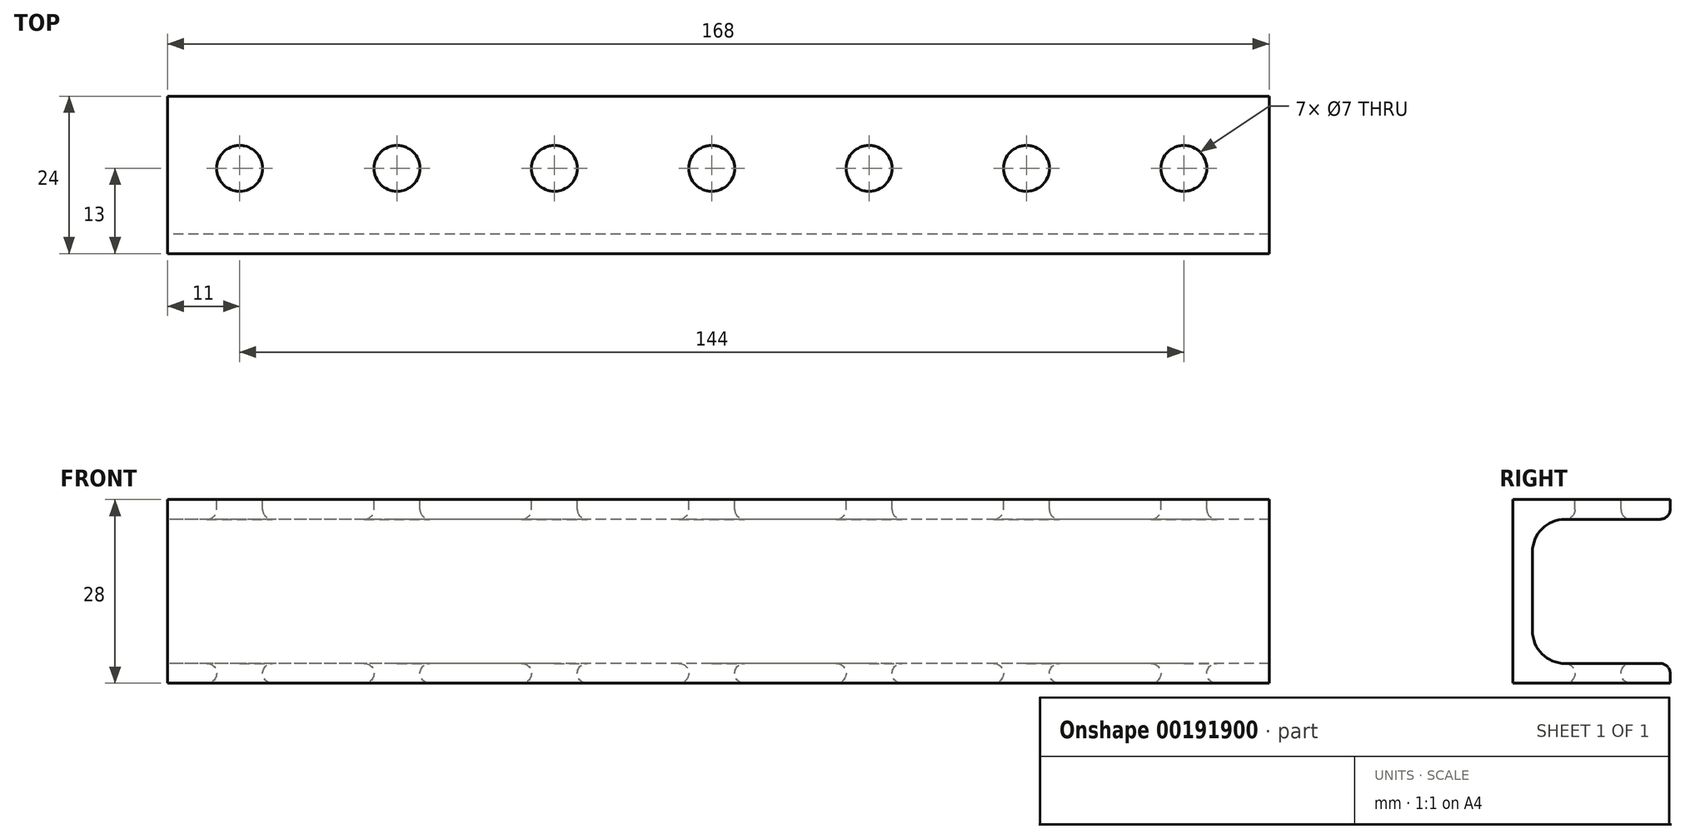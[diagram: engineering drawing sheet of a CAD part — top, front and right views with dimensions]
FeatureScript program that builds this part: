
annotation { "Feature Type Name" : "Feature", "Feature Type Description" : "" }
export const myFeature = defineFeature(function(context is Context, id is Id, definition is map)
    precondition{}
    {
        {
            var Q0;
            Q0=qCreatedBy(makeId("Right.planeOp"),FACE);
            var sketch = newSketch(context, id + "F0", { "sketchPlane" : qUnion([Q0])});
            skLineSegment(sketch, "E0", {"start": v(0, 27.91) * mm, "end": v(24, 27.91) * mm});
            skLineSegment(sketch, "E1", {"start": v(24, 27.91) * mm, "end": v(24, 24.91) * mm});
            skLineSegment(sketch, "E2", {"start": v(24, 24.91) * mm, "end": v(3, 24.91) * mm});
            skLineSegment(sketch, "E3", {"start": v(3, 24.91) * mm, "end": v(3, 2.91) * mm});
            skLineSegment(sketch, "E4", {"start": v(3, 2.91) * mm, "end": v(24, 2.91) * mm});
            skLineSegment(sketch, "E5", {"start": v(24, 2.91) * mm, "end": v(24, -0.09) * mm});
            skLineSegment(sketch, "E6", {"start": v(24, -0.09) * mm, "end": v(0, -0.09) * mm});
            skLineSegment(sketch, "E7", {"start": v(0, -0.09) * mm, "end": v(0, 0) * mm});
            skLineSegment(sketch, "E8", {"start": v(0, 27.91) * mm, "end": v(0, -0.09) * mm});
            skSolve(sketch);
        }
        {
            var Q0;
            {var subQ0=sQuery(id+"F0.wireOp",EDGE,"E0");Q0=makeQuery(id+"F0.imprint","IMPRINT",FACE,{"disambiguationData":[TD([[makeQuery(id+"F0.imprint","IMPRINT",EDGE,{"derivedFrom":subQ0}),-1.0]])]});}
            extrude(context, id + "F1", {"entities" : qUnion([Q0]), "depth" : 168 * mm});
        }
        {
            var Q0;
            Q0=makeQuery(id+"F1.opExtrude","SWEPT_FACE",FACE,{"disambiguationData":[OSD([sQuery(id+"F0.wireOp",EDGE,"E0")])]});
            var sketch = newSketch(context, id + "F2", { "sketchPlane" : qUnion([Q0])});
            skCircle(sketch, "E9", {"center": v(11, 13) * mm, "radius": 3.5 * mm});
            skCircle(sketch, "E10.1.0.0", {"center": v(35, 13) * mm, "radius": 3.5 * mm});
            skCircle(sketch, "E10.2.0.0", {"center": v(59, 13) * mm, "radius": 3.5 * mm});
            skCircle(sketch, "E10.3.0.0", {"center": v(83, 13) * mm, "radius": 3.5 * mm});
            skCircle(sketch, "E10.4.0.0", {"center": v(107, 13) * mm, "radius": 3.5 * mm});
            skCircle(sketch, "E10.5.0.0", {"center": v(131, 13) * mm, "radius": 3.5 * mm});
            skCircle(sketch, "E10.6.0.0", {"center": v(155, 13) * mm, "radius": 3.5 * mm});
            skLineSegment(sketch, "E10.direction1", {"start": v(11, 13) * mm, "end": v(35, 13) * mm, "construction": true});
            skSolve(sketch);
        }
        {
            var Q0;
            Q0=makeQuery(id+"F2.imprint","IMPRINT",FACE,{"disambiguationData":[TD([[makeQuery(id+"F2.imprint","IMPRINT",EDGE,{"derivedFrom":sQuery(id+"F2.wireOp",EDGE,"E9")}),1.0]])]});
            var Q1;
            Q1=makeQuery(id+"F2.imprint","IMPRINT",FACE,{"disambiguationData":[TD([[makeQuery(id+"F2.imprint","IMPRINT",EDGE,{"derivedFrom":sQuery(id+"F2.wireOp",EDGE,"E10.1.0.0")}),1.0]])]});
            var Q2;
            Q2=makeQuery(id+"F2.imprint","IMPRINT",FACE,{"disambiguationData":[TD([[makeQuery(id+"F2.imprint","IMPRINT",EDGE,{"derivedFrom":sQuery(id+"F2.wireOp",EDGE,"E10.2.0.0")}),1.0]])]});
            var Q3;
            Q3=makeQuery(id+"F2.imprint","IMPRINT",FACE,{"disambiguationData":[TD([[makeQuery(id+"F2.imprint","IMPRINT",EDGE,{"derivedFrom":sQuery(id+"F2.wireOp",EDGE,"E10.3.0.0")}),1.0]])]});
            var Q4;
            Q4=makeQuery(id+"F2.imprint","IMPRINT",FACE,{"disambiguationData":[TD([[makeQuery(id+"F2.imprint","IMPRINT",EDGE,{"derivedFrom":sQuery(id+"F2.wireOp",EDGE,"E10.4.0.0")}),1.0]])]});
            var Q5;
            Q5=makeQuery(id+"F2.imprint","IMPRINT",FACE,{"disambiguationData":[TD([[makeQuery(id+"F2.imprint","IMPRINT",EDGE,{"derivedFrom":sQuery(id+"F2.wireOp",EDGE,"E10.5.0.0")}),1.0]])]});
            var Q6;
            Q6=makeQuery(id+"F2.imprint","IMPRINT",FACE,{"disambiguationData":[TD([[makeQuery(id+"F2.imprint","IMPRINT",EDGE,{"derivedFrom":sQuery(id+"F2.wireOp",EDGE,"E10.6.0.0")}),1.0]])]});
            extrude(context, id + "F3", {"entities" : qUnion([Q0, Q1, Q2, Q3, Q4, Q5, Q6]), "operationType" : NewBodyOperationType.REMOVE, "oppositeDirection" : true, "depth" : 33 * mm});
        }
        {
            var Q0;
            Q0=makeQuery(id+"F1.opExtrude","SWEPT_EDGE",EDGE,{"disambiguationData":[OSD([sQuery(id+"F0.wireOp",EDGE,"E2"),sQuery(id+"F0.wireOp",EDGE,"E3")])]});
            var Q1;
            Q1=makeQuery(id+"F1.opExtrude","SWEPT_EDGE",EDGE,{"disambiguationData":[OSD([sQuery(id+"F0.wireOp",EDGE,"E3"),sQuery(id+"F0.wireOp",EDGE,"E4")])]});
            fillet(context, id + "F4", {"entities" : qUnion([Q0, Q1]), "radius" : 5 * mm, "tangentPropagation" : true, "allowEdgeOverflow" : false});
        }
        {
            var Q0;
            Q0=makeQuery(id+"F1.opExtrude","SWEPT_EDGE",EDGE,{"disambiguationData":[OSD([sQuery(id+"F0.wireOp",EDGE,"E1"),sQuery(id+"F0.wireOp",EDGE,"E2")])]});
            var Q1;
            Q1=makeQuery(id+"F1.opExtrude","SWEPT_EDGE",EDGE,{"disambiguationData":[OSD([sQuery(id+"F0.wireOp",EDGE,"E4"),sQuery(id+"F0.wireOp",EDGE,"E5")])]});
            fillet(context, id + "F5", {"entities" : qUnion([Q0, Q1]), "radius" : 1.5 * mm, "tangentPropagation" : true, "allowEdgeOverflow" : false});
        }
        {
            var Q0;
            Q0=makeQuery(id+"F3.boolean.opBoolean","COPY",EDGE,{"derivedFrom":makeQuery(id+"F3.opExtrude","CAP_EDGE",EDGE,{"disambiguationData":[OSD([sQuery(id+"F2.wireOp",EDGE,"E9")])],"isStart":true})});
            var Q1;
            Q1=makeQuery(id+"F3.boolean.opBoolean","INTERSECT",EDGE,{"derivedFrom":[makeQuery(id+"F1.opExtrude","SWEPT_FACE",FACE,{"disambiguationData":[OSD([sQuery(id+"F0.wireOp",EDGE,"E2")])]}),makeQuery(id+"F3.opExtrude","SWEPT_FACE",FACE,{"disambiguationData":[OSD([sQuery(id+"F2.wireOp",EDGE,"E9")])]})]});
            fillet(context, id + "F6", {"entities" : qUnion([Q0, Q1]), "radius" : 1.5 * mm, "tangentPropagation" : true, "allowEdgeOverflow" : false});
        }
        {
            var Q0;
            Q0=makeQuery(id+"F3.boolean.opBoolean","INTERSECT",EDGE,{"derivedFrom":[makeQuery(id+"F1.opExtrude","SWEPT_FACE",FACE,{"disambiguationData":[OSD([sQuery(id+"F0.wireOp",EDGE,"E2")])]}),makeQuery(id+"F3.opExtrude","SWEPT_FACE",FACE,{"disambiguationData":[OSD([sQuery(id+"F2.wireOp",EDGE,"E10.1.0.0")])]})]});
            var Q1;
            Q1=makeQuery(id+"F3.boolean.opBoolean","COPY",EDGE,{"derivedFrom":makeQuery(id+"F3.opExtrude","CAP_EDGE",EDGE,{"disambiguationData":[OSD([sQuery(id+"F2.wireOp",EDGE,"E10.1.0.0")])],"isStart":true})});
            var Q2;
            Q2=makeQuery(id+"F3.boolean.opBoolean","INTERSECT",EDGE,{"derivedFrom":[makeQuery(id+"F1.opExtrude","SWEPT_FACE",FACE,{"disambiguationData":[OSD([sQuery(id+"F0.wireOp",EDGE,"E2")])]}),makeQuery(id+"F3.opExtrude","SWEPT_FACE",FACE,{"disambiguationData":[OSD([sQuery(id+"F2.wireOp",EDGE,"E10.2.0.0")])]})]});
            var Q3;
            Q3=makeQuery(id+"F3.boolean.opBoolean","COPY",EDGE,{"derivedFrom":makeQuery(id+"F3.opExtrude","CAP_EDGE",EDGE,{"disambiguationData":[OSD([sQuery(id+"F2.wireOp",EDGE,"E10.2.0.0")])],"isStart":true})});
            var Q4;
            Q4=makeQuery(id+"F3.boolean.opBoolean","INTERSECT",EDGE,{"derivedFrom":[makeQuery(id+"F1.opExtrude","SWEPT_FACE",FACE,{"disambiguationData":[OSD([sQuery(id+"F0.wireOp",EDGE,"E2")])]}),makeQuery(id+"F3.opExtrude","SWEPT_FACE",FACE,{"disambiguationData":[OSD([sQuery(id+"F2.wireOp",EDGE,"E10.3.0.0")])]})]});
            var Q5;
            Q5=makeQuery(id+"F3.boolean.opBoolean","COPY",EDGE,{"derivedFrom":makeQuery(id+"F3.opExtrude","CAP_EDGE",EDGE,{"disambiguationData":[OSD([sQuery(id+"F2.wireOp",EDGE,"E10.3.0.0")])],"isStart":true})});
            var Q6;
            Q6=makeQuery(id+"F3.boolean.opBoolean","INTERSECT",EDGE,{"derivedFrom":[makeQuery(id+"F1.opExtrude","SWEPT_FACE",FACE,{"disambiguationData":[OSD([sQuery(id+"F0.wireOp",EDGE,"E2")])]}),makeQuery(id+"F3.opExtrude","SWEPT_FACE",FACE,{"disambiguationData":[OSD([sQuery(id+"F2.wireOp",EDGE,"E10.4.0.0")])]})]});
            var Q7;
            Q7=makeQuery(id+"F3.boolean.opBoolean","COPY",EDGE,{"derivedFrom":makeQuery(id+"F3.opExtrude","CAP_EDGE",EDGE,{"disambiguationData":[OSD([sQuery(id+"F2.wireOp",EDGE,"E10.4.0.0")])],"isStart":true})});
            var Q8;
            Q8=makeQuery(id+"F3.boolean.opBoolean","INTERSECT",EDGE,{"derivedFrom":[makeQuery(id+"F1.opExtrude","SWEPT_FACE",FACE,{"disambiguationData":[OSD([sQuery(id+"F0.wireOp",EDGE,"E2")])]}),makeQuery(id+"F3.opExtrude","SWEPT_FACE",FACE,{"disambiguationData":[OSD([sQuery(id+"F2.wireOp",EDGE,"E10.5.0.0")])]})]});
            var Q9;
            Q9=makeQuery(id+"F3.boolean.opBoolean","COPY",EDGE,{"derivedFrom":makeQuery(id+"F3.opExtrude","CAP_EDGE",EDGE,{"disambiguationData":[OSD([sQuery(id+"F2.wireOp",EDGE,"E10.5.0.0")])],"isStart":true})});
            var Q10;
            Q10=makeQuery(id+"F3.boolean.opBoolean","INTERSECT",EDGE,{"derivedFrom":[makeQuery(id+"F1.opExtrude","SWEPT_FACE",FACE,{"disambiguationData":[OSD([sQuery(id+"F0.wireOp",EDGE,"E2")])]}),makeQuery(id+"F3.opExtrude","SWEPT_FACE",FACE,{"disambiguationData":[OSD([sQuery(id+"F2.wireOp",EDGE,"E10.6.0.0")])]})]});
            var Q11;
            Q11=makeQuery(id+"F3.boolean.opBoolean","COPY",EDGE,{"derivedFrom":makeQuery(id+"F3.opExtrude","CAP_EDGE",EDGE,{"disambiguationData":[OSD([sQuery(id+"F2.wireOp",EDGE,"E10.6.0.0")])],"isStart":true})});
            fillet(context, id + "F7", {"entities" : qUnion([Q0, Q1, Q2, Q3, Q4, Q5, Q6, Q7, Q8, Q9, Q10, Q11]), "radius" : 1.5 * mm, "tangentPropagation" : true, "allowEdgeOverflow" : false});
        }
        {
            var Q0;
            Q0=makeQuery(id+"F3.boolean.opBoolean","INTERSECT",EDGE,{"derivedFrom":[makeQuery(id+"F1.opExtrude","SWEPT_FACE",FACE,{"disambiguationData":[OSD([sQuery(id+"F0.wireOp",EDGE,"E6")])]}),makeQuery(id+"F3.opExtrude","SWEPT_FACE",FACE,{"disambiguationData":[OSD([sQuery(id+"F2.wireOp",EDGE,"E9")])]})]});
            var Q1;
            Q1=makeQuery(id+"F3.boolean.opBoolean","INTERSECT",EDGE,{"derivedFrom":[makeQuery(id+"F1.opExtrude","SWEPT_FACE",FACE,{"disambiguationData":[OSD([sQuery(id+"F0.wireOp",EDGE,"E4")])]}),makeQuery(id+"F3.opExtrude","SWEPT_FACE",FACE,{"disambiguationData":[OSD([sQuery(id+"F2.wireOp",EDGE,"E9")])]})]});
            var Q2;
            Q2=makeQuery(id+"F3.boolean.opBoolean","INTERSECT",EDGE,{"derivedFrom":[makeQuery(id+"F1.opExtrude","SWEPT_FACE",FACE,{"disambiguationData":[OSD([sQuery(id+"F0.wireOp",EDGE,"E6")])]}),makeQuery(id+"F3.opExtrude","SWEPT_FACE",FACE,{"disambiguationData":[OSD([sQuery(id+"F2.wireOp",EDGE,"E10.1.0.0")])]})]});
            var Q3;
            Q3=makeQuery(id+"F3.boolean.opBoolean","INTERSECT",EDGE,{"derivedFrom":[makeQuery(id+"F1.opExtrude","SWEPT_FACE",FACE,{"disambiguationData":[OSD([sQuery(id+"F0.wireOp",EDGE,"E4")])]}),makeQuery(id+"F3.opExtrude","SWEPT_FACE",FACE,{"disambiguationData":[OSD([sQuery(id+"F2.wireOp",EDGE,"E10.1.0.0")])]})]});
            var Q4;
            Q4=makeQuery(id+"F3.boolean.opBoolean","INTERSECT",EDGE,{"derivedFrom":[makeQuery(id+"F1.opExtrude","SWEPT_FACE",FACE,{"disambiguationData":[OSD([sQuery(id+"F0.wireOp",EDGE,"E6")])]}),makeQuery(id+"F3.opExtrude","SWEPT_FACE",FACE,{"disambiguationData":[OSD([sQuery(id+"F2.wireOp",EDGE,"E10.2.0.0")])]})]});
            var Q5;
            Q5=makeQuery(id+"F3.boolean.opBoolean","INTERSECT",EDGE,{"derivedFrom":[makeQuery(id+"F1.opExtrude","SWEPT_FACE",FACE,{"disambiguationData":[OSD([sQuery(id+"F0.wireOp",EDGE,"E4")])]}),makeQuery(id+"F3.opExtrude","SWEPT_FACE",FACE,{"disambiguationData":[OSD([sQuery(id+"F2.wireOp",EDGE,"E10.2.0.0")])]})]});
            var Q6;
            Q6=makeQuery(id+"F3.boolean.opBoolean","INTERSECT",EDGE,{"derivedFrom":[makeQuery(id+"F1.opExtrude","SWEPT_FACE",FACE,{"disambiguationData":[OSD([sQuery(id+"F0.wireOp",EDGE,"E6")])]}),makeQuery(id+"F3.opExtrude","SWEPT_FACE",FACE,{"disambiguationData":[OSD([sQuery(id+"F2.wireOp",EDGE,"E10.3.0.0")])]})]});
            var Q7;
            Q7=makeQuery(id+"F3.boolean.opBoolean","INTERSECT",EDGE,{"derivedFrom":[makeQuery(id+"F1.opExtrude","SWEPT_FACE",FACE,{"disambiguationData":[OSD([sQuery(id+"F0.wireOp",EDGE,"E4")])]}),makeQuery(id+"F3.opExtrude","SWEPT_FACE",FACE,{"disambiguationData":[OSD([sQuery(id+"F2.wireOp",EDGE,"E10.3.0.0")])]})]});
            var Q8;
            Q8=makeQuery(id+"F3.boolean.opBoolean","INTERSECT",EDGE,{"derivedFrom":[makeQuery(id+"F1.opExtrude","SWEPT_FACE",FACE,{"disambiguationData":[OSD([sQuery(id+"F0.wireOp",EDGE,"E6")])]}),makeQuery(id+"F3.opExtrude","SWEPT_FACE",FACE,{"disambiguationData":[OSD([sQuery(id+"F2.wireOp",EDGE,"E10.4.0.0")])]})]});
            var Q9;
            Q9=makeQuery(id+"F3.boolean.opBoolean","INTERSECT",EDGE,{"derivedFrom":[makeQuery(id+"F1.opExtrude","SWEPT_FACE",FACE,{"disambiguationData":[OSD([sQuery(id+"F0.wireOp",EDGE,"E4")])]}),makeQuery(id+"F3.opExtrude","SWEPT_FACE",FACE,{"disambiguationData":[OSD([sQuery(id+"F2.wireOp",EDGE,"E10.4.0.0")])]})]});
            var Q10;
            Q10=makeQuery(id+"F3.boolean.opBoolean","INTERSECT",EDGE,{"derivedFrom":[makeQuery(id+"F1.opExtrude","SWEPT_FACE",FACE,{"disambiguationData":[OSD([sQuery(id+"F0.wireOp",EDGE,"E6")])]}),makeQuery(id+"F3.opExtrude","SWEPT_FACE",FACE,{"disambiguationData":[OSD([sQuery(id+"F2.wireOp",EDGE,"E10.5.0.0")])]})]});
            var Q11;
            Q11=makeQuery(id+"F3.boolean.opBoolean","INTERSECT",EDGE,{"derivedFrom":[makeQuery(id+"F1.opExtrude","SWEPT_FACE",FACE,{"disambiguationData":[OSD([sQuery(id+"F0.wireOp",EDGE,"E4")])]}),makeQuery(id+"F3.opExtrude","SWEPT_FACE",FACE,{"disambiguationData":[OSD([sQuery(id+"F2.wireOp",EDGE,"E10.5.0.0")])]})]});
            var Q12;
            Q12=makeQuery(id+"F3.boolean.opBoolean","INTERSECT",EDGE,{"derivedFrom":[makeQuery(id+"F1.opExtrude","SWEPT_FACE",FACE,{"disambiguationData":[OSD([sQuery(id+"F0.wireOp",EDGE,"E6")])]}),makeQuery(id+"F3.opExtrude","SWEPT_FACE",FACE,{"disambiguationData":[OSD([sQuery(id+"F2.wireOp",EDGE,"E10.6.0.0")])]})]});
            var Q13;
            Q13=makeQuery(id+"F3.boolean.opBoolean","INTERSECT",EDGE,{"derivedFrom":[makeQuery(id+"F1.opExtrude","SWEPT_FACE",FACE,{"disambiguationData":[OSD([sQuery(id+"F0.wireOp",EDGE,"E4")])]}),makeQuery(id+"F3.opExtrude","SWEPT_FACE",FACE,{"disambiguationData":[OSD([sQuery(id+"F2.wireOp",EDGE,"E10.6.0.0")])]})]});
            fillet(context, id + "F8", {"entities" : qUnion([Q0, Q1, Q2, Q3, Q4, Q5, Q6, Q7, Q8, Q9, Q10, Q11, Q12, Q13]), "radius" : 1.5 * mm, "tangentPropagation" : true, "allowEdgeOverflow" : false});
        }
    });
